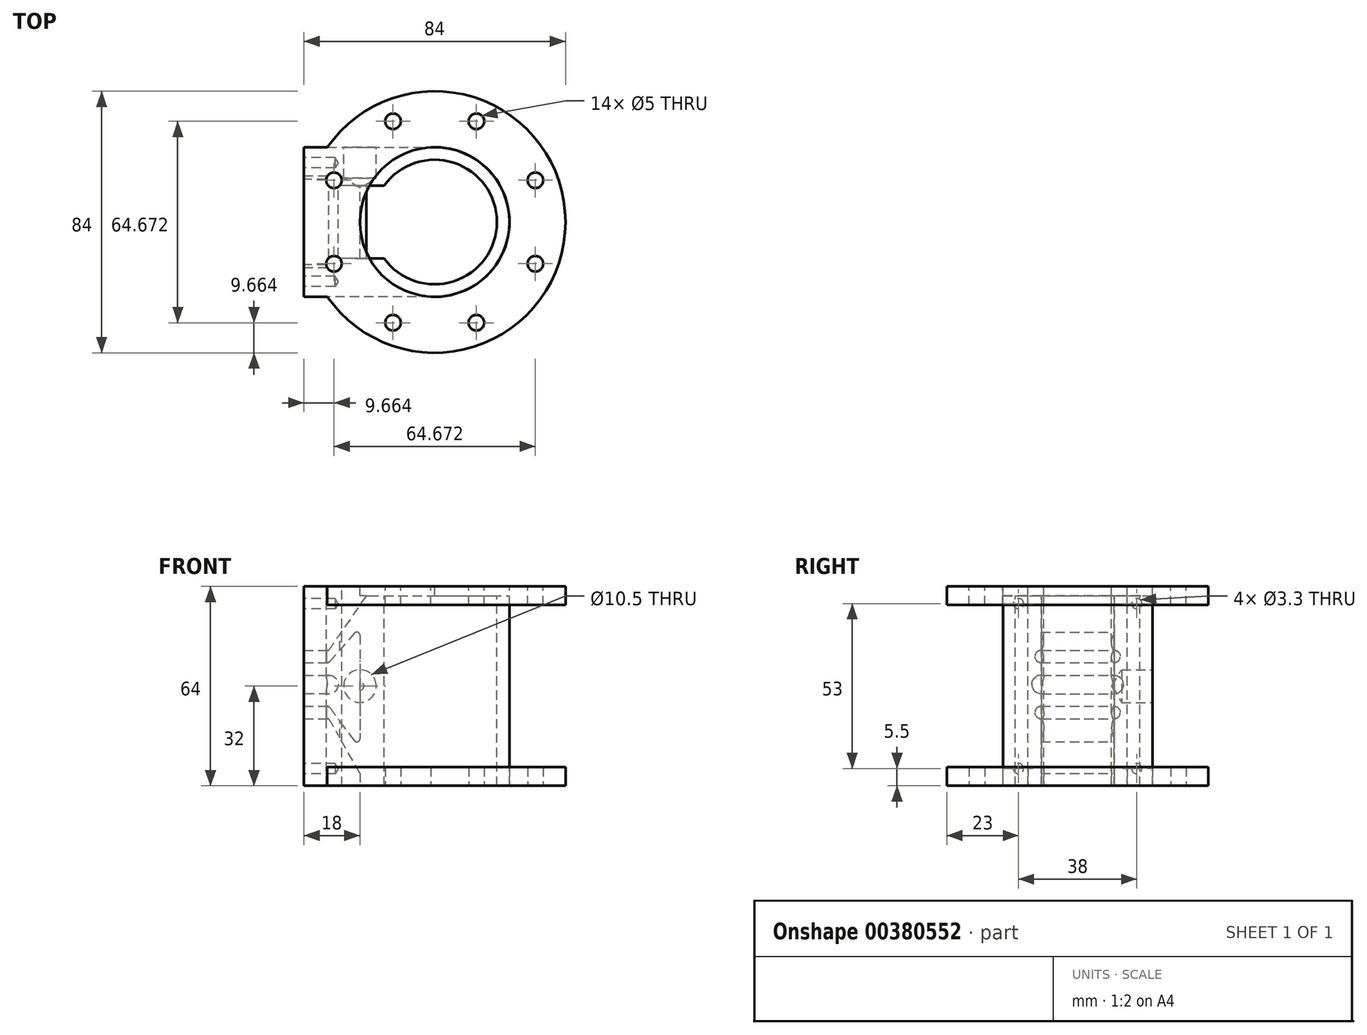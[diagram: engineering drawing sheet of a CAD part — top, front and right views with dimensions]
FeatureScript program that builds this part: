
annotation { "Feature Type Name" : "Feature", "Feature Type Description" : "" }
export const myFeature = defineFeature(function(context is Context, id is Id, definition is map)
    precondition{}
    {
        {
            var Q0;
            Q0=qCreatedBy(makeId("Top.planeOp"),FACE);
            var sketch = newSketch(context, id + "F0", { "sketchPlane" : qUnion([Q0])});
            skArc(sketch, "E0", {"start": v(-34.47, -24) * mm, "mid": v(42, 0) * mm, "end": v(-34.47, 24) * mm});
            skCircle(sketch, "E1", {"center": v(0, 0) * mm, "radius": 20 * mm});
            skCircle(sketch, "E2", {"center": v(0, 0) * mm, "radius": 35 * mm, "construction": true});
            skLineSegment(sketch, "E3", {"start": v(0, 71.76) * mm, "end": v(0, 20) * mm, "construction": true});
            skLineSegment(sketch, "E4", {"start": v(-64.72, 0) * mm, "end": v(-10.92, 0) * mm, "construction": true});
            skLineSegment(sketch, "E5", {"start": v(-12.55, 5.2) * mm, "end": v(-110.75, 45.87) * mm, "construction": true});
            skLineSegment(sketch, "E6", {"start": v(-7.65, 18.48) * mm, "end": v(-42.73, 103.16) * mm, "construction": true});
            skCircle(sketch, "E7", {"center": v(-32.34, 13.4) * mm, "radius": 2.5 * mm});
            skCircle(sketch, "E8", {"center": v(-13.4, 32.34) * mm, "radius": 2.5 * mm});
            skCircle(sketch, "E9.MirrorC", {"center": v(13.4, 32.34) * mm, "radius": 2.5 * mm});
            skCircle(sketch, "E10.MirrorC", {"center": v(32.34, 13.4) * mm, "radius": 2.5 * mm});
            skCircle(sketch, "E11.MirrorC", {"center": v(32.34, -13.4) * mm, "radius": 2.5 * mm});
            skCircle(sketch, "E12.MirrorC", {"center": v(13.4, -32.34) * mm, "radius": 2.5 * mm});
            skCircle(sketch, "E13.MirrorC", {"center": v(-13.4, -32.34) * mm, "radius": 2.5 * mm});
            skCircle(sketch, "E14.MirrorC", {"center": v(-32.34, -13.4) * mm, "radius": 2.5 * mm});
            skCircle(sketch, "E15", {"center": v(0, 0) * mm, "radius": 24 * mm});
            skLineSegment(sketch, "E16", {"start": v(0, 24) * mm, "end": v(-42, 24) * mm});
            skLineSegment(sketch, "E17", {"start": v(0, 24) * mm, "end": v(0, -24) * mm, "construction": true});
            skLineSegment(sketch, "E18", {"start": v(0, -24) * mm, "end": v(-42, -24) * mm});
            skLineSegment(sketch, "E19", {"start": v(-42, -24) * mm, "end": v(-42, 24) * mm});
            skLineSegment(sketch, "E20", {"start": v(-19.69, 3.53) * mm, "end": v(-38.39, 3.53) * mm, "construction": true});
            skLineSegment(sketch, "E21", {"start": v(-38.39, 3.53) * mm, "end": v(-38.39, -3.53) * mm, "construction": true});
            skLineSegment(sketch, "E22", {"start": v(-38.39, -3.53) * mm, "end": v(-19.69, -3.53) * mm, "construction": true});
            skPoint(sketch, "E23", {"position": v(-38.39, 0) * mm});
            skCircle(sketch, "E24", {"center": v(-20, 0) * mm, "radius": 9.08 * mm, "construction": true});
            skLineSegment(sketch, "E25.bottom", {"start": v(-42, -21) * mm, "end": v(-32.3, -21) * mm, "construction": true});
            skLineSegment(sketch, "E25.top", {"start": v(-42, -17.1) * mm, "end": v(-32.3, -17.1) * mm, "construction": true});
            skLineSegment(sketch, "E25.left", {"start": v(-42, -21) * mm, "end": v(-42, -17.1) * mm, "construction": true});
            skLineSegment(sketch, "E25.right", {"start": v(-32.3, -21) * mm, "end": v(-32.3, -17.1) * mm, "construction": true});
            skLineSegment(sketch, "E26.bottom", {"start": v(-42, 21.16) * mm, "end": v(-32.38, 21.16) * mm, "construction": true});
            skLineSegment(sketch, "E26.top", {"start": v(-42, 17.49) * mm, "end": v(-32.38, 17.49) * mm, "construction": true});
            skLineSegment(sketch, "E26.left", {"start": v(-42, 21.16) * mm, "end": v(-42, 17.49) * mm});
            skLineSegment(sketch, "E26.right", {"start": v(-32.38, 21.16) * mm, "end": v(-32.38, 17.49) * mm, "construction": true});
            skLineSegment(sketch, "E27.bottom", {"start": v(-34.59, 9.94) * mm, "end": v(-30.32, 9.94) * mm, "construction": true});
            skLineSegment(sketch, "E27.top", {"start": v(-34.59, -9.9) * mm, "end": v(-30.32, -9.9) * mm, "construction": true});
            skLineSegment(sketch, "E27.left", {"start": v(-34.59, 9.94) * mm, "end": v(-34.59, -9.9) * mm, "construction": true});
            skLineSegment(sketch, "E27.right", {"start": v(-30.32, 9.94) * mm, "end": v(-30.32, -9.9) * mm, "construction": true});
            skLineSegment(sketch, "E28.trimOffspring", {"start": v(0, 0) * mm, "end": v(0, -71.76) * mm, "construction": true});
            skLineSegment(sketch, "E29.trimOffspring", {"start": v(20, 0) * mm, "end": v(64.72, 0) * mm, "construction": true});
            skSolve(sketch);
        }
        {
            var Q0;
            Q0=qCreatedBy(makeId("Front.planeOp"),FACE);
            var sketch = newSketch(context, id + "F1", { "sketchPlane" : qUnion([Q0])});
            skLineSegment(sketch, "E30.bottom", {"start": v(-42, 0) * mm, "end": v(42, 0) * mm, "construction": true});
            skLineSegment(sketch, "E30.top", {"start": v(-42, -64) * mm, "end": v(42, -64) * mm, "construction": true});
            skLineSegment(sketch, "E30.left", {"start": v(-42, 0) * mm, "end": v(-42, -64) * mm, "construction": true});
            skLineSegment(sketch, "E30.right", {"start": v(42, 0) * mm, "end": v(42, -64) * mm, "construction": true});
            skLineSegment(sketch, "E31.bottom", {"start": v(-42, 0) * mm, "end": v(42, 0) * mm});
            skLineSegment(sketch, "E31.top", {"start": v(-42, -6) * mm, "end": v(42, -6) * mm});
            skLineSegment(sketch, "E31.left", {"start": v(-42, 0) * mm, "end": v(-42, -6) * mm});
            skLineSegment(sketch, "E31.right", {"start": v(42, 0) * mm, "end": v(42, -6) * mm});
            skLineSegment(sketch, "E32.bottom", {"start": v(-42, -58) * mm, "end": v(42, -58) * mm});
            skLineSegment(sketch, "E32.top", {"start": v(-42, -64) * mm, "end": v(42, -64) * mm});
            skLineSegment(sketch, "E32.left", {"start": v(-42, -58) * mm, "end": v(-42, -64) * mm});
            skLineSegment(sketch, "E32.right", {"start": v(42, -58) * mm, "end": v(42, -64) * mm});
            skLineSegment(sketch, "E33", {"start": v(-24, 0) * mm, "end": v(24, 0) * mm});
            skLineSegment(sketch, "E34", {"start": v(-24, 0) * mm, "end": v(-24, -64) * mm, "construction": true});
            skLineSegment(sketch, "E35", {"start": v(24, 0) * mm, "end": v(24, -64) * mm, "construction": true});
            skLineSegment(sketch, "E36", {"start": v(-20, 0) * mm, "end": v(-20, -64) * mm, "construction": true});
            skLineSegment(sketch, "E37", {"start": v(20.03, 0) * mm, "end": v(20.03, -58) * mm, "construction": true});
            skSolve(sketch);
        }
        {
            var Q0;
            Q0=makeQuery(id+"F0.imprint","IMPRINT",FACE,{"disambiguationData":[TD([[makeQuery(id+"F0.imprint","IMPRINT",EDGE,{"derivedFrom":sQuery(id+"F0.wireOp",EDGE,"E1")}),-1.0]])]});
            var Q1;
            Q1=makeQuery(id+"F0.imprint","IMPRINT",FACE,{"disambiguationData":[TD([[makeQuery(id+"F0.imprint","IMPRINT",EDGE,{"derivedFrom":sQuery(id+"F0.wireOp",EDGE,"E7")}),-1.0]])]});
            extrude(context, id + "F2", {"entities" : qUnion([Q0, Q1]), "oppositeDirection" : true, "depth" : 64 * mm});
        }
        {
            var Q0;
            Q0=qCreatedBy(makeId("Top.planeOp"),FACE);
            var sketch = newSketch(context, id + "F3", { "sketchPlane" : qUnion([Q0])});
            skArc(sketch, "E38", {"start": v(-34.47, -24) * mm, "mid": v(42, 0) * mm, "end": v(-34.47, 24) * mm});
            skLineSegment(sketch, "E39", {"start": v(-20, 0) * mm, "end": v(-20, 0) * mm});
            skLineSegment(sketch, "E40", {"start": v(-142.95, 0) * mm, "end": v(-116.62, 0) * mm, "construction": true});
            skCircle(sketch, "E41", {"center": v(-32.34, 13.4) * mm, "radius": 2.5 * mm});
            skCircle(sketch, "E42", {"center": v(-13.4, 32.34) * mm, "radius": 2.5 * mm});
            skCircle(sketch, "E43.MirrorC", {"center": v(13.4, 32.34) * mm, "radius": 2.5 * mm});
            skCircle(sketch, "E44.MirrorC", {"center": v(32.34, 13.4) * mm, "radius": 2.5 * mm});
            skCircle(sketch, "E45.MirrorC", {"center": v(32.34, -13.4) * mm, "radius": 2.5 * mm});
            skCircle(sketch, "E46.MirrorC", {"center": v(13.4, -32.34) * mm, "radius": 2.5 * mm});
            skCircle(sketch, "E47.MirrorC", {"center": v(-13.4, -32.34) * mm, "radius": 2.5 * mm});
            skCircle(sketch, "E48.MirrorC", {"center": v(-32.34, -13.4) * mm, "radius": 2.5 * mm});
            skLineSegment(sketch, "E49", {"start": v(0, 24) * mm, "end": v(0, 24) * mm});
            skLineSegment(sketch, "E50", {"start": v(-34.47, -24) * mm, "end": v(-42, -24) * mm});
            skLineSegment(sketch, "E51", {"start": v(-42, -24) * mm, "end": v(-42, 24) * mm});
            skLineSegment(sketch, "E52", {"start": v(-116.62, 3.53) * mm, "end": v(-116.62, -3.53) * mm, "construction": true});
            skPoint(sketch, "E53", {"position": v(-116.62, 0) * mm});
            skLineSegment(sketch, "E54.left", {"start": v(-42, -2.64) * mm, "end": v(-42, 1.25) * mm, "construction": true});
            skLineSegment(sketch, "E55.bottom", {"start": v(-112.82, 28.3) * mm, "end": v(-108.56, 28.3) * mm, "construction": true});
            skLineSegment(sketch, "E55.top", {"start": v(-112.82, 8.44) * mm, "end": v(-108.56, 8.44) * mm, "construction": true});
            skLineSegment(sketch, "E55.left", {"start": v(-112.82, 28.3) * mm, "end": v(-112.82, 8.44) * mm, "construction": true});
            skLineSegment(sketch, "E55.right", {"start": v(-108.56, 28.3) * mm, "end": v(-108.56, 8.44) * mm, "construction": true});
            skPoint(sketch, "E56.orphan", {"position": v(0, 53.4) * mm});
            skLineSegment(sketch, "E57.trimOffspring", {"start": v(0, -42) * mm, "end": v(0, -53.4) * mm, "construction": true});
            skLineSegment(sketch, "E58.trimOffspring", {"start": v(-34.47, 24) * mm, "end": v(-42, 24) * mm});
            skPoint(sketch, "E59.trimOffspring.end.orphan", {"position": v(142.95, 0) * mm});
            skCircle(sketch, "E60", {"center": v(0, 0) * mm, "radius": 24.03 * mm});
            skSolve(sketch);
        }
        {
            var Q0;
            Q0=makeQuery(id+"F3.imprint","IMPRINT",FACE,{"disambiguationData":[TD([[makeQuery(id+"F3.imprint","IMPRINT",EDGE,{"derivedFrom":sQuery(id+"F3.wireOp",EDGE,"E38")}),1.0]])]});
            extrude(context, id + "F4", {"entities" : qUnion([Q0]), "operationType" : NewBodyOperationType.ADD, "oppositeDirection" : true, "depth" : 6 * mm});
        }
        {
            var Q0;
            Q0=makeQuery(id+"F2.opExtrude","CAP_FACE",FACE,{"disambiguationData":[OSD([sQuery(id+"F0.wireOp",EDGE,"E1"),sQuery(id+"F0.wireOp",EDGE,"E15")])],"isStart":false});
            var sketch = newSketch(context, id + "F5", { "sketchPlane" : qUnion([Q0])});
            skArc(sketch, "E61.0", {"start": v(0, 24) * mm, "mid": v(24, 0) * mm, "end": v(0, -24) * mm});
            skLineSegment(sketch, "E61.1.0", {"start": v(-1.29, -24) * mm, "end": v(-34.47, -24) * mm});
            skArc(sketch, "E61.1.1", {"start": v(-34.47, -24) * mm, "mid": v(42, 0) * mm, "end": v(-34.47, 24) * mm});
            skLineSegment(sketch, "E61.1.2", {"start": v(-34.47, 24) * mm, "end": v(-1.29, 24) * mm});
            skArc(sketch, "E61.1.3", {"start": v(-1.29, 24) * mm, "mid": v(24.03, 0) * mm, "end": v(-1.29, -24) * mm});
            skCircle(sketch, "E62.0", {"center": v(13.4, 32.34) * mm, "radius": 2.5 * mm});
            skCircle(sketch, "E62.1", {"center": v(-13.4, 32.34) * mm, "radius": 2.5 * mm});
            skCircle(sketch, "E62.3", {"center": v(32.34, 13.4) * mm, "radius": 2.5 * mm});
            skCircle(sketch, "E62.4", {"center": v(32.34, -13.4) * mm, "radius": 2.5 * mm});
            skCircle(sketch, "E62.5", {"center": v(13.4, -32.34) * mm, "radius": 2.5 * mm});
            skCircle(sketch, "E62.7", {"center": v(-13.4, -32.34) * mm, "radius": 2.5 * mm});
            skSolve(sketch);
        }
        {
            var Q0;
            Q0=makeQuery(id+"F5.imprint","IMPRINT",FACE,{"disambiguationData":[TD([[makeQuery(id+"F5.imprint","IMPRINT",EDGE,{"derivedFrom":sQuery(id+"F5.wireOp",EDGE,"E61.1.0")}),1.0]])]});
            extrude(context, id + "F6", {"entities" : qUnion([Q0]), "operationType" : NewBodyOperationType.ADD, "oppositeDirection" : true, "depth" : 6 * mm});
        }
        {
            var Q0;
            Q0=makeQuery(id+"F2.opExtrude","SWEPT_FACE",FACE,{"disambiguationData":[OSD([sQuery(id+"F0.wireOp",EDGE,"E19"),sQuery(id+"F0.wireOp",EDGE,"E26.left")])]});
            var sketch = newSketch(context, id + "F7", { "sketchPlane" : qUnion([Q0])});
            skCircle(sketch, "E63", {"center": v(-19, -5.5) * mm, "radius": 2.65 * mm});
            skCircle(sketch, "E64.MirrorC", {"center": v(19, -5.5) * mm, "radius": 2.65 * mm});
            skLineSegment(sketch, "E65", {"start": v(0, 0) * mm, "end": v(0, -64) * mm, "construction": true});
            skLineSegment(sketch, "E66", {"start": v(60.89, -32) * mm, "end": v(-49.42, -32) * mm, "construction": true});
            skPoint(sketch, "E66.startSnap0", {"position": v(0, -32) * mm});
            skCircle(sketch, "E67.MirrorC", {"center": v(-19, -58.5) * mm, "radius": 2.65 * mm});
            skCircle(sketch, "E68.MirrorC", {"center": v(19, -58.5) * mm, "radius": 2.65 * mm});
            skSolve(sketch);
        }
        {
            var Q0;
            Q0=sQuery(id+"F7.wireOp",VERTEX,"E63.center");
            var Q1;
            Q1=sQuery(id+"F7.wireOp",VERTEX,"E64.MirrorC.center");
            var Q2;
            Q2=sQuery(id+"F7.wireOp",VERTEX,"E67.MirrorC.center");
            var Q3;
            Q3=sQuery(id+"F7.wireOp",VERTEX,"E68.MirrorC.center");
            var Q4;
            Q4=makeQuery(id+"F2.opExtrude","SWEPT_BODY",BODY,{"disambiguationData":[OSD([sQuery(id+"F0.wireOp",EDGE,"E1"),sQuery(id+"F0.wireOp",EDGE,"E7"),sQuery(id+"F0.wireOp",EDGE,"E14.MirrorC"),sQuery(id+"F0.wireOp",EDGE,"E15"),sQuery(id+"F0.wireOp",EDGE,"E16"),sQuery(id+"F0.wireOp",EDGE,"E18"),sQuery(id+"F0.wireOp",EDGE,"E19"),sQuery(id+"F0.wireOp",EDGE,"E26.left")])]});
            hole(context, id + "F8", {"style" : HoleStyle.SIMPLE, "endStyle" : HoleEndStyle.BLIND, "holeDiameter" : 3.3 * mm, "holeDepth" : 10 * mm, "tappedDepth" : 12.7 * mm, "tapClearance" : 3, "locations" : qUnion([Q0, Q1, Q2, Q3]), "scope" : qUnion([Q4])});
        }
        {
            var Q0;
            Q0=makeQuery(id+"F0.imprint","IMPRINT",FACE,{"disambiguationData":[TD([[makeQuery(id+"F0.imprint","IMPRINT",EDGE,{"derivedFrom":sQuery(id+"F0.wireOp",EDGE,"E1")}),-1.0]])]});
            extrude(context, id + "F9", {"entities" : qUnion([Q0]), "operationType" : NewBodyOperationType.REMOVE, "oppositeDirection" : true, "depth" : 3 * mm});
        }
        {
            var Q0;
            Q0=qCreatedBy(makeId("Front.planeOp"),FACE);
            cPlane(context, id + "F10", {"entities" : qUnion([Q0]), "cplaneType" : CPlaneType.OFFSET, "offset" : 55.7 * mm, "oppositeDirection" : true, "width" : 150 * mm, "height" : 150 * mm});
        }
        {
            var Q0;
            Q0=qCreatedBy(id+"F10.planeOp",FACE);
            var sketch = newSketch(context, id + "F11", { "sketchPlane" : qUnion([Q0])});
            skLineSegment(sketch, "E69.bottom", {"start": v(-63.22, 16.05) * mm, "end": v(57.63, 16.05) * mm});
            skLineSegment(sketch, "E69.top", {"start": v(-63.22, -69.82) * mm, "end": v(57.63, -69.82) * mm});
            skLineSegment(sketch, "E69.left", {"start": v(-63.22, 16.05) * mm, "end": v(-63.22, -69.82) * mm});
            skLineSegment(sketch, "E69.right", {"start": v(57.63, 16.05) * mm, "end": v(57.63, -69.82) * mm});
            skSolve(sketch);
        }
        {
            var Q0;
            Q0=makeQuery(id+"F11.imprint","IMPRINT",FACE,{"disambiguationData":[TD([[makeQuery(id+"F11.imprint","IMPRINT",EDGE,{"derivedFrom":sQuery(id+"F11.wireOp",EDGE,"E69.bottom")}),-1.0]])]});
            extrude(context, id + "F12", {"entities" : qUnion([Q0]), "operationType" : NewBodyOperationType.REMOVE, "depth" : 55.4 * mm});
        }
        {
            var Q0;
            {var subQ4=sQuery(id+"F0.wireOp",EDGE,"E15");Q0=makeQuery(id+"F12.boolean.opBoolean","COPY",FACE,{"disambiguationData":[TD([makeQuery(id+"F9.boolean.opBoolean","COPY",FACE,{"derivedFrom":makeQuery(id+"F9.opExtrude","SWEPT_FACE",FACE,{"disambiguationData":[OSD([subQ4])]})})])],"derivedFrom":makeQuery(id+"F12.opExtrude","CAP_FACE",FACE,{"disambiguationData":[OSD([sQuery(id+"F11.wireOp",EDGE,"E69.bottom"),sQuery(id+"F11.wireOp",EDGE,"E69.top"),sQuery(id+"F11.wireOp",EDGE,"E69.left"),sQuery(id+"F11.wireOp",EDGE,"E69.right")])],"isStart":false})});}
            var sketch = newSketch(context, id + "F13", { "sketchPlane" : qUnion([Q0])});
            skLineSegment(sketch, "E70", {"start": v(24, -15.66) * mm, "end": v(24, -48.92) * mm});
            skLineSegment(sketch, "E71", {"start": v(42, -28.5) * mm, "end": v(34, -28.5) * mm});
            skLineSegment(sketch, "E72", {"start": v(34, -28.5) * mm, "end": v(34, -34.5) * mm, "construction": true});
            skLineSegment(sketch, "E73", {"start": v(34, -34.5) * mm, "end": v(42, -34.5) * mm});
            skLineSegment(sketch, "E74", {"start": v(24, -60) * mm, "end": v(24, -64) * mm});
            skArc(sketch, "E75", {"start": v(34, -28.5) * mm, "mid": v(31, -31.5) * mm, "end": v(34, -34.5) * mm});
            skLineSegment(sketch, "E76.bottom", {"start": v(42, -20.5) * mm, "end": v(34, -20.5) * mm});
            skLineSegment(sketch, "E76.top", {"start": v(42, -24.5) * mm, "end": v(34.46, -24.5) * mm});
            skLineSegment(sketch, "E76.left", {"start": v(42, -20.5) * mm, "end": v(42, -24.5) * mm});
            skLineSegment(sketch, "E76.right", {"start": v(34, -20.5) * mm, "end": v(34, -24.5) * mm, "construction": true});
            skLineSegment(sketch, "E77.bottom", {"start": v(42, -38.5) * mm, "end": v(34.5, -38.5) * mm});
            skLineSegment(sketch, "E77.top", {"start": v(42, -42.5) * mm, "end": v(34, -42.5) * mm});
            skLineSegment(sketch, "E77.left", {"start": v(42, -38.5) * mm, "end": v(42, -42.5) * mm});
            skLineSegment(sketch, "E77.right", {"start": v(34, -38.5) * mm, "end": v(34, -42.5) * mm, "construction": true});
            skLineSegment(sketch, "E78", {"start": v(22, -3) * mm, "end": v(34, -20.5) * mm});
            skLineSegment(sketch, "E79", {"start": v(24, -60) * mm, "end": v(34, -42.5) * mm});
            skLineSegment(sketch, "E80", {"start": v(25.75, -15) * mm, "end": v(33.7, -24.16) * mm});
            skLineSegment(sketch, "E81", {"start": v(25.8, -49.52) * mm, "end": v(33.7, -38.9) * mm});
            skPoint(sketch, "E82.visualSharp", {"position": v(24, -12.99) * mm});
            skArc(sketch, "E82.filletArc", {"start": v(25.75, -15) * mm, "mid": v(24.65, -14.73) * mm, "end": v(24, -15.66) * mm});
            skPoint(sketch, "E83.visualSharp", {"position": v(24, -51.94) * mm});
            skArc(sketch, "E83.filletArc", {"start": v(24, -48.92) * mm, "mid": v(24.68, -49.87) * mm, "end": v(25.8, -49.52) * mm});
            skPoint(sketch, "E84.visualSharp", {"position": v(34, -24.5) * mm});
            skArc(sketch, "E84.filletArc", {"start": v(33.7, -24.16) * mm, "mid": v(34.04, -24.4) * mm, "end": v(34.46, -24.5) * mm});
            skPoint(sketch, "E85.visualSharp", {"position": v(34, -38.5) * mm});
            skArc(sketch, "E85.filletArc", {"start": v(34.5, -38.5) * mm, "mid": v(34.05, -38.6) * mm, "end": v(33.7, -38.9) * mm});
            skLineSegment(sketch, "E86", {"start": v(22, -3) * mm, "end": v(20, -3) * mm});
            skLineSegment(sketch, "E87", {"start": v(20, -64) * mm, "end": v(24, -64) * mm});
            skLineSegment(sketch, "E88", {"start": v(42, -42.5) * mm, "end": v(42, -20.5) * mm});
            skLineSegment(sketch, "E89", {"start": v(16.24, -3) * mm, "end": v(16.24, -64) * mm});
            skLineSegment(sketch, "E90", {"start": v(16.24, -3) * mm, "end": v(20, -3) * mm});
            skLineSegment(sketch, "E91", {"start": v(16.24, -64) * mm, "end": v(20, -64) * mm});
            skSolve(sketch);
        }
        {
            var Q0;
            Q0=makeQuery(id+"F13.imprint","IMPRINT",FACE,{"disambiguationData":[TD([[makeQuery(id+"F13.imprint","IMPRINT",EDGE,{"derivedFrom":sQuery(id+"F13.wireOp",EDGE,"E70")}),-1.0]])]});
            var Q1;
            {var subQ0=sQuery(id+"F13.wireOp",EDGE,"E71");Q1=makeQuery(id+"F13.imprint","IMPRINT",FACE,{"disambiguationData":[TD([[makeQuery(id+"F13.imprint","IMPRINT",EDGE,{"derivedFrom":subQ0}),1.0]])]});}
            var Q2;
            Q2=makeQuery(id+"F13.imprint","IMPRINT",FACE,{"disambiguationData":[TD([[makeQuery(id+"F13.imprint","IMPRINT",EDGE,{"derivedFrom":sQuery(id+"F13.wireOp",EDGE,"E89")}),1.0]])]});
            extrude(context, id + "F14", {"entities" : qUnion([Q0, Q1, Q2]), "operationType" : NewBodyOperationType.REMOVE, "oppositeDirection" : true, "depth" : 12 * mm});
        }
        {
            var Q0;
            Q0=makeQuery(id+"F2.opExtrude","SWEPT_BODY",BODY,{"disambiguationData":[OSD([sQuery(id+"F0.wireOp",EDGE,"E1"),sQuery(id+"F0.wireOp",EDGE,"E7"),sQuery(id+"F0.wireOp",EDGE,"E14.MirrorC"),sQuery(id+"F0.wireOp",EDGE,"E15"),sQuery(id+"F0.wireOp",EDGE,"E16"),sQuery(id+"F0.wireOp",EDGE,"E18"),sQuery(id+"F0.wireOp",EDGE,"E19"),sQuery(id+"F0.wireOp",EDGE,"E26.left")])]});
            var Q1;
            Q1=qCreatedBy(makeId("Front.planeOp"),FACE);
            mirror(context, id + "F15", {"operationType" : NewBodyOperationType.ADD, "entities" : qUnion([Q0]), "mirrorPlane" : qUnion([Q1])});
        }
        {
            var Q0;
            {var subQ0=makeQuery(id+"F2.opExtrude","SWEPT_FACE",FACE,{"disambiguationData":[OSD([sQuery(id+"F0.wireOp",EDGE,"E19"),sQuery(id+"F0.wireOp",EDGE,"E26.left")])]});Q0=makeQuery(id+"F15.boolean.opBoolean","MERGE",FACE,{"derivedFrom":[subQ0,makeQuery(id+"F15.opPattern","COPY",FACE,{"derivedFrom":subQ0,"instanceName":"1"})]});}
            var sketch = newSketch(context, id + "F16", { "sketchPlane" : qUnion([Q0])});
            skArc(sketch, "E92", {"start": v(-11.7, -20.5) * mm, "mid": v(-13.7, -22.5) * mm, "end": v(-11.7, -24.5) * mm});
            skArc(sketch, "E93", {"start": v(11.7, -24.5) * mm, "mid": v(13.7, -22.5) * mm, "end": v(11.7, -20.5) * mm});
            skArc(sketch, "E94", {"start": v(11.7, -34.5) * mm, "mid": v(14.7, -31.5) * mm, "end": v(11.7, -28.5) * mm});
            skArc(sketch, "E95", {"start": v(-11.7, -28.5) * mm, "mid": v(-14.7, -31.5) * mm, "end": v(-11.7, -34.5) * mm});
            skArc(sketch, "E96", {"start": v(-11.7, -38.5) * mm, "mid": v(-13.7, -40.5) * mm, "end": v(-11.7, -42.5) * mm});
            skArc(sketch, "E97", {"start": v(11.7, -42.5) * mm, "mid": v(13.7, -40.5) * mm, "end": v(11.7, -38.5) * mm});
            skLineSegment(sketch, "E98", {"start": v(-11.7, -28.5) * mm, "end": v(11.7, -28.5) * mm});
            skLineSegment(sketch, "E99", {"start": v(11.7, -34.5) * mm, "end": v(-11.7, -34.5) * mm});
            skLineSegment(sketch, "E100", {"start": v(-11.7, -38.5) * mm, "end": v(11.7, -38.5) * mm});
            skLineSegment(sketch, "E101", {"start": v(11.7, -42.5) * mm, "end": v(-11.7, -42.5) * mm});
            skLineSegment(sketch, "E102", {"start": v(-11.7, -34.5) * mm, "end": v(11.7, -34.5) * mm});
            skLineSegment(sketch, "E103", {"start": v(-11.7, -24.5) * mm, "end": v(11.7, -24.5) * mm});
            skLineSegment(sketch, "E104", {"start": v(-11.7, -20.5) * mm, "end": v(11.7, -20.5) * mm});
            skSolve(sketch);
        }
        {
            var Q0;
            Q0=makeQuery(id+"F16.imprint","IMPRINT",FACE,{"disambiguationData":[TD([[makeQuery(id+"F16.imprint","IMPRINT",EDGE,{"derivedFrom":sQuery(id+"F16.wireOp",EDGE,"E92")}),1.0]])]});
            var Q1;
            Q1=makeQuery(id+"F16.imprint","IMPRINT",FACE,{"disambiguationData":[TD([[makeQuery(id+"F16.imprint","IMPRINT",EDGE,{"derivedFrom":sQuery(id+"F16.wireOp",EDGE,"E93")}),1.0]])]});
            var Q2;
            Q2=makeQuery(id+"F16.imprint","IMPRINT",FACE,{"disambiguationData":[TD([[makeQuery(id+"F16.imprint","IMPRINT",EDGE,{"derivedFrom":sQuery(id+"F16.wireOp",EDGE,"E95")}),1.0]])]});
            var Q3;
            Q3=makeQuery(id+"F16.imprint","IMPRINT",FACE,{"disambiguationData":[TD([[makeQuery(id+"F16.imprint","IMPRINT",EDGE,{"derivedFrom":sQuery(id+"F16.wireOp",EDGE,"E94")}),1.0]])]});
            var Q4;
            Q4=makeQuery(id+"F16.imprint","IMPRINT",FACE,{"disambiguationData":[TD([[makeQuery(id+"F16.imprint","IMPRINT",EDGE,{"derivedFrom":sQuery(id+"F16.wireOp",EDGE,"E96")}),1.0]])]});
            var Q5;
            Q5=makeQuery(id+"F16.imprint","IMPRINT",FACE,{"disambiguationData":[TD([[makeQuery(id+"F16.imprint","IMPRINT",EDGE,{"derivedFrom":sQuery(id+"F16.wireOp",EDGE,"E97")}),1.0]])]});
            extrude(context, id + "F17", {"entities" : qUnion([Q0, Q1, Q2, Q3, Q4, Q5]), "operationType" : NewBodyOperationType.REMOVE, "oppositeDirection" : true, "depth" : 10 * mm});
        }
        {
            var Q0;
            Q0=makeQuery(id+"F15.opPattern","COPY",FACE,{"derivedFrom":makeQuery(id+"F2.opExtrude","SWEPT_FACE",FACE,{"disambiguationData":[OSD([sQuery(id+"F0.wireOp",EDGE,"E18")])]}),"instanceName":"1"});
            var sketch = newSketch(context, id + "F18", { "sketchPlane" : qUnion([Q0])});
            skCircle(sketch, "E105.0", {"center": v(24, -32) * mm, "radius": 5.25 * mm});
            skSolve(sketch);
        }
        {
            var Q0;
            Q0=sQuery(id+"F18.wireOp",VERTEX,"E105.0.center");
            var Q1;
            Q1=makeQuery(id+"F2.opExtrude","SWEPT_BODY",BODY,{"disambiguationData":[OSD([sQuery(id+"F0.wireOp",EDGE,"E1"),sQuery(id+"F0.wireOp",EDGE,"E7"),sQuery(id+"F0.wireOp",EDGE,"E14.MirrorC"),sQuery(id+"F0.wireOp",EDGE,"E15"),sQuery(id+"F0.wireOp",EDGE,"E16"),sQuery(id+"F0.wireOp",EDGE,"E18"),sQuery(id+"F0.wireOp",EDGE,"E19"),sQuery(id+"F0.wireOp",EDGE,"E26.left")])]});
            hole(context, id + "F19", {"style" : HoleStyle.SIMPLE, "endStyle" : HoleEndStyle.BLIND, "holeDiameter" : 10.5 * mm, "holeDepth" : 9.9 * mm, "isTappedThrough" : true, "tappedDepth" : 12.7 * mm, "tapClearance" : 3, "locations" : qUnion([Q0]), "scope" : qUnion([Q1])});
        }
    });
